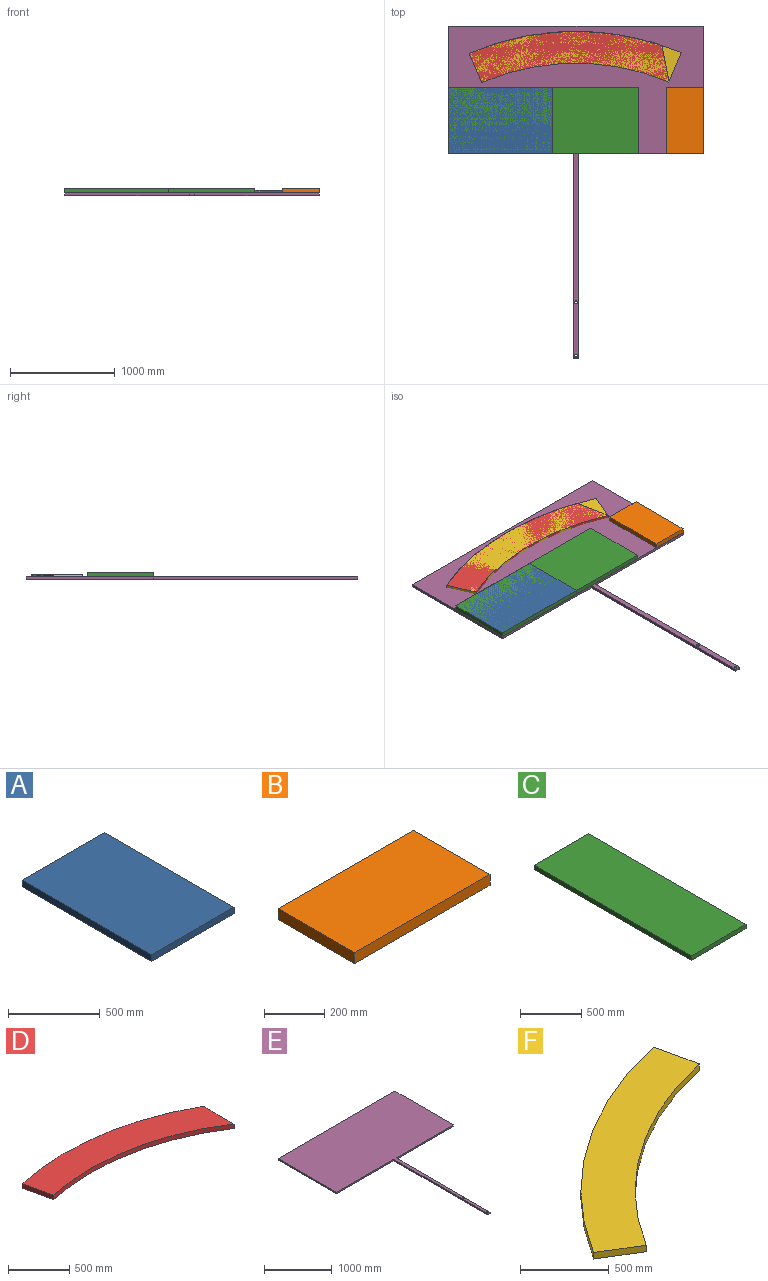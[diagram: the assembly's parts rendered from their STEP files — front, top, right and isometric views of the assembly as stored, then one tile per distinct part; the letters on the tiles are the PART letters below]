
ASSEMBLY  parts=6 mates=6
PART A: 6 faces, bbox 635x995.8x44.5 mm
  f0: plane 635x44.45mm, normal (0,1,0), area 28225.7mm2, adj f1,f3,f4,f5
  f1: plane 995.75x44.45mm, normal (-1,0,0), area 44261.2mm2, adj f0,f2,f4,f5
  f2: plane 635x44.45mm, normal (0,-1,0), area 28225.7mm2, adj f1,f3,f4,f5
  f3: plane 995.75x44.45mm, normal (1,0,0), area 44261.2mm2, adj f0,f2,f4,f5
  f4: plane 995.75x635mm, normal (0,0,-1), area 632302.5mm2, adj f0,f1,f2,f3
  f5: plane 995.75x635mm, normal (0,0,1), area 632302.5mm2, adj f0,f1,f2,f3
PART B: 6 faces, bbox 635x357.4x44.5 mm
  f0: plane 635x44.45mm, normal (0,1,0), area 28225.7mm2, adj f1,f3,f4,f5
  f1: plane 357.41x44.45mm, normal (-1,0,0), area 15886.9mm2, adj f0,f2,f4,f5
  f2: plane 635x44.45mm, normal (0,-1,0), area 28225.7mm2, adj f1,f3,f4,f5
  f3: plane 357.41x44.45mm, normal (1,0,0), area 15886.9mm2, adj f0,f2,f4,f5
  f4: plane 635x357.41mm, normal (0,0,1), area 226955.9mm2, adj f0,f1,f2,f3
  f5: plane 635x357.41mm, normal (0,0,-1), area 226955.9mm2, adj f0,f1,f2,f3
PART C: 6 faces, bbox 635x1821.2x44.5 mm
  f0: plane 1821.22x44.45mm, normal (-1,0,0), area 80953.3mm2, adj f1,f3,f4,f5
  f1: plane 635x44.45mm, normal (0,-1,0), area 28225.7mm2, adj f0,f2,f4,f5
  f2: plane 1821.22x44.45mm, normal (1,0,0), area 80953.3mm2, adj f1,f3,f4,f5
  f3: plane 635x44.45mm, normal (0,1,0), area 28225.7mm2, adj f0,f2,f4,f5
  f4: plane 1821.22x635mm, normal (0,0,-1), area 1156475.3mm2, adj f0,f1,f2,f3
  f5: plane 1821.22x635mm, normal (0,0,1), area 1156475.3mm2, adj f0,f1,f2,f3
PART D: 6 faces, bbox 1825.6x690x44.5 mm
  f0: plane 357.41x44.45mm, normal (1,0,0), area 15886.9mm2, adj f1,f3,f4,f5
  f1: cylinder r=2590.8mm len=1825.57mm, axis (0,0,-1), area 83887.1mm2, adj f0,f2,f4,f5
  f2: plane 297.71x65.36mm, normal (-0.98,-0.21,0), area 13548.4mm2, adj f1,f3,f4,f5
  f3: cylinder r=2286mm len=1760.21mm, axis (0,0,-1), area 81813.4mm2, adj f0,f2,f4,f5
  f4: plane 1825.57x690.04mm, normal (0,0,1), area 567893.3mm2, adj f0,f1,f2,f3
  f5: plane 1825.57x690.04mm, normal (0,0,-1), area 567893.3mm2, adj f0,f1,f2,f3
PART E: 12 faces, bbox 2438.4x3175x25.4 mm
  f0: plane 1193.8x25.4mm, normal (0,-1,0), area 30322.5mm2, adj f1,f8,f10,f11
  f1: plane 1955.8x25.4mm, normal (-1,0,0), area 49677.3mm2, adj f0,f2,f10,f11
  f2: plane 50.8x25.4mm, normal (0,-1,0), area 1290.3mm2, adj f1,f3,f10,f11
  f3: plane 1955.8x25.4mm, normal (1,0,0), area 49677.3mm2, adj f2,f4,f10,f11
  f4: plane 1193.8x25.4mm, normal (0,-1,0), area 30322.5mm2, adj f3,f5,f10,f11
  f5: plane 1219.2x25.4mm, normal (1,0,0), area 30967.7mm2, adj f4,f6,f10,f11
  f6: plane 2438.4x25.4mm, normal (0,1,0), area 61935.4mm2, adj f5,f8,f10,f11
  f7: cylinder r=12.7mm len=25.4mm, axis (0,0,-1), area 2026.8mm2, adj f10,f11
  f8: plane 1219.2x25.4mm, normal (-1,0,0), area 30967.7mm2, adj f0,f6,f10,f11
  f9: cylinder r=12.7mm len=25.4mm, axis (0,0,-1), area 2026.8mm2, adj f10,f11
  f10: plane 3175x2438.4mm, normal (0,0,1), area 3071238.5mm2, adj f0,f1,f2,f3,f4,f5,f6,f7
  f11: plane 3175x2438.4mm, normal (0,0,-1), area 3071238.5mm2, adj f0,f1,f2,f3,f4,f5,f6,f7
PART F: 6 faces, bbox 1719.1x1336.6x44.5 mm
  f0: plane 297.71x65.36mm, normal (0.98,0.21,0), area 13548.4mm2, adj f1,f3,f4,f5
  f1: cylinder r=2590.8mm len=1653.79mm, axis (0,0,-1), area 92721.9mm2, adj f0,f2,f4,f5
  f2: plane 259.92x159.19mm, normal (-0.52,-0.85,0), area 13548.4mm2, adj f1,f3,f4,f5
  f3: cylinder r=2286mm len=1459.22mm, axis (0,0,-1), area 81813.4mm2, adj f0,f2,f4,f5
  f4: plane 1719.15x1336.59mm, normal (0,0,1), area 598406.6mm2, adj f0,f1,f2,f3
  f5: plane 1719.15x1336.59mm, normal (0,0,-1), area 598406.6mm2, adj f0,f1,f2,f3
PLACE A rot(axis=(0,0,1),90deg) t=(-92.27,-1308.63,-679.45)mm
PLACE B rot(axis=(0,0,1),90deg) t=(1988.72,-1308.63,-1028.7)mm
PLACE C rot(axis=(0,0,1),90deg) t=(-1088.02,-1308.63,-679.45)mm
PLACE D rot(axis=(0,0,1),10.9deg) t=(-1131.24,-1461.03,-1047.75)mm
PLACE E at identity fixed
PLACE F rot(axis=(0,0,-1),35.3deg) t=(-1131.24,-1461.03,-1047.75)mm
MATE revolute D.f3 <-> E.f7  axis (0,0,1) through (-1131.24,-1461.03,50.8)mm
MATE revolute F.f4 <-> D.f4  axis (0,0,1) through (-2153.52,919.56,50.8)mm
MATE revolute F.f3 <-> E.f7  axis (0,0,1) through (-1131.24,-1461.03,50.8)mm
MATE fastened E.f10 <-> B.f5  axis (0,0,1) through (87.96,-38.63,25.4)mm
MATE fastened A.f4 <-> E.f10  axis (0,0,-1) through (-2350.44,-38.63,25.4)mm
MATE fastened C.f4 <-> E.f10  axis (0,0,-1) through (-2350.44,-38.63,25.4)mm
